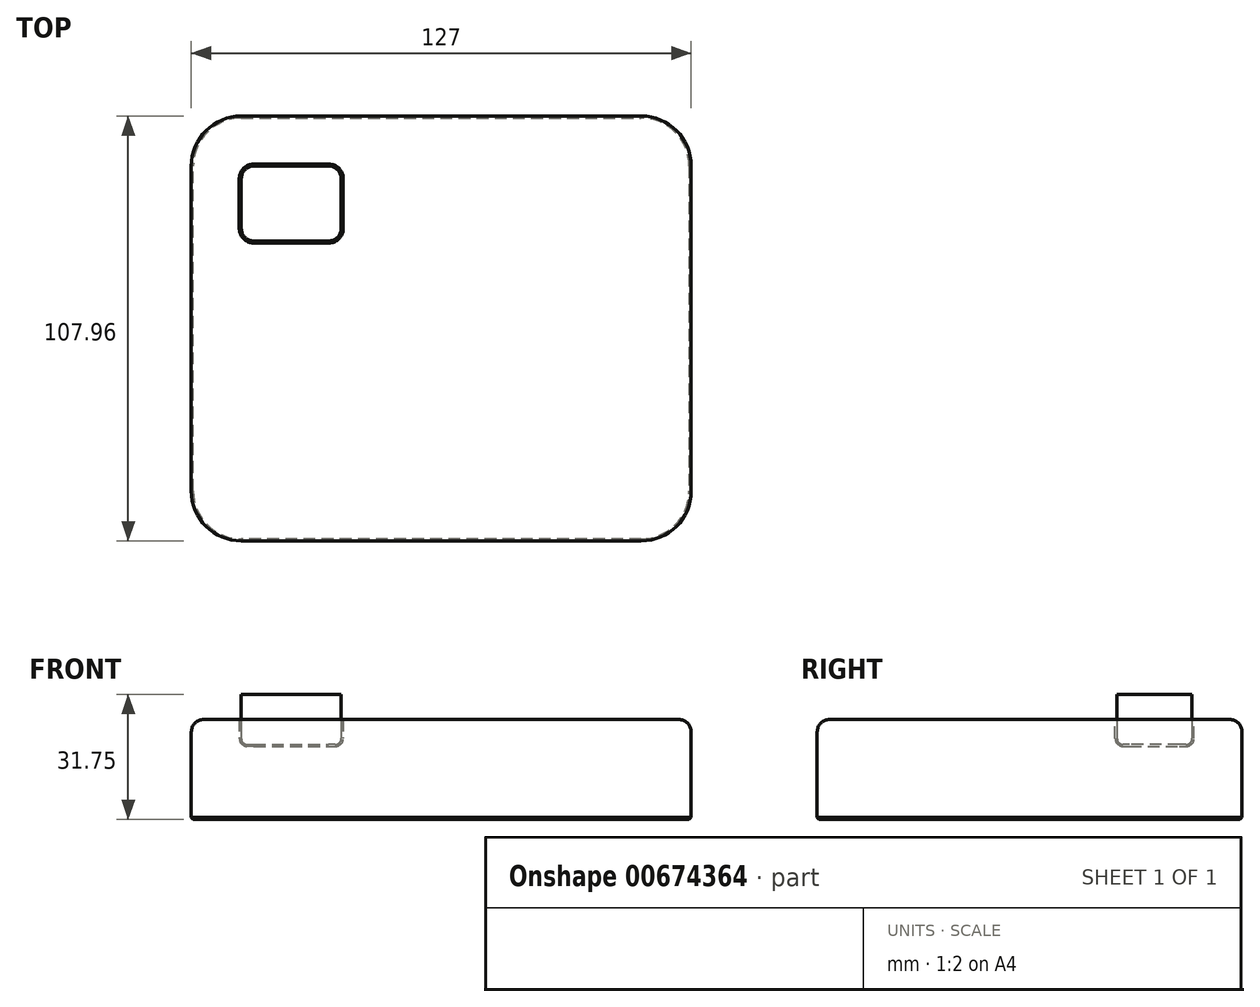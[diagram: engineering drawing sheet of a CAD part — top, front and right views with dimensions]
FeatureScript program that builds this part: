
annotation { "Feature Type Name" : "Feature", "Feature Type Description" : "" }
export const myFeature = defineFeature(function(context is Context, id is Id, definition is map)
    precondition{}
    {
        {
            var Q0;
            Q0=qCreatedBy(makeId("Top.planeOp"),FACE);
            var sketch = newSketch(context, id + "F0", { "sketchPlane" : qUnion([Q0])});
            skLineSegment(sketch, "E0.bottom", {"start": v(63.5, 53.98) * mm, "end": v(-63.5, 53.98) * mm});
            skLineSegment(sketch, "E0.top", {"start": v(63.5, -53.97) * mm, "end": v(-63.5, -53.97) * mm});
            skLineSegment(sketch, "E0.left", {"start": v(63.5, 53.98) * mm, "end": v(63.5, -53.98) * mm});
            skLineSegment(sketch, "E0.right", {"start": v(-63.5, 53.98) * mm, "end": v(-63.5, -53.97) * mm});
            skPoint(sketch, "E0.middle", {"position": v(0, 0) * mm});
            skSolve(sketch);
        }
        {
            var Q0;
            Q0=makeQuery(id+"F0.imprint","IMPRINT",FACE,{"disambiguationData":[TD([[makeQuery(id+"F0.imprint","IMPRINT",EDGE,{"derivedFrom":sQuery(id+"F0.wireOp",EDGE,"E0.bottom")}),1.0]])]});
            extrude(context, id + "F1", {"entities" : qUnion([Q0]), "depth" : 25.4 * mm});
        }
        {
            var Q0;
            Q0=makeQuery(id+"F1.opExtrude","CAP_FACE",FACE,{"disambiguationData":[OSD([sQuery(id+"F0.wireOp",EDGE,"E0.bottom"),sQuery(id+"F0.wireOp",EDGE,"E0.top"),sQuery(id+"F0.wireOp",EDGE,"E0.left"),sQuery(id+"F0.wireOp",EDGE,"E0.right")])],"isStart":false});
            var sketch = newSketch(context, id + "F2", { "sketchPlane" : qUnion([Q0])});
            skLineSegment(sketch, "E1.bottom", {"start": v(-50.8, 41.28) * mm, "end": v(-25.4, 41.28) * mm});
            skLineSegment(sketch, "E1.top", {"start": v(-50.8, 22.23) * mm, "end": v(-25.4, 22.23) * mm});
            skLineSegment(sketch, "E1.left", {"start": v(-50.8, 41.28) * mm, "end": v(-50.8, 22.23) * mm});
            skLineSegment(sketch, "E1.right", {"start": v(-25.4, 41.28) * mm, "end": v(-25.4, 22.23) * mm});
            skSolve(sketch);
        }
        {
            var Q0;
            Q0=qSketchRegion(id+"F2",true);
            extrude(context, id + "F3", {"entities" : qUnion([Q0]), "depth" : 12.7 * mm, "offsetDistance" : 25.4 * mm, "symmetric" : true});
        }
        {
            var Q0;
            Q0=makeQuery(id+"F3.opExtrude","SWEPT_EDGE",EDGE,{"disambiguationData":[OSD([sQuery(id+"F2.wireOp",EDGE,"E1.bottom"),sQuery(id+"F2.wireOp",EDGE,"E1.right")])]});
            var Q1;
            Q1=makeQuery(id+"F3.opExtrude","SWEPT_EDGE",EDGE,{"disambiguationData":[OSD([sQuery(id+"F2.wireOp",EDGE,"E1.top"),sQuery(id+"F2.wireOp",EDGE,"E1.right")])]});
            var Q2;
            Q2=makeQuery(id+"F3.opExtrude","SWEPT_EDGE",EDGE,{"disambiguationData":[OSD([sQuery(id+"F2.wireOp",EDGE,"E1.top"),sQuery(id+"F2.wireOp",EDGE,"E1.left")])]});
            var Q3;
            Q3=makeQuery(id+"F3.opExtrude","SWEPT_EDGE",EDGE,{"disambiguationData":[OSD([sQuery(id+"F2.wireOp",EDGE,"E1.bottom"),sQuery(id+"F2.wireOp",EDGE,"E1.left")])]});
            fillet(context, id + "F4", {"entities" : qUnion([Q0, Q1, Q2, Q3]), "radius" : 3.17 * mm, "tangentPropagation" : true, "allowEdgeOverflow" : false});
        }
        {
            var Q0;
            Q0=makeQuery(id+"F3.opExtrude","CAP_EDGE",EDGE,{"disambiguationData":[OSD([sQuery(id+"F2.wireOp",EDGE,"E1.top")])],"isStart":true});
            fillet(context, id + "F5", {"entities" : qUnion([Q0]), "radius" : 1.52 * mm, "tangentPropagation" : true, "allowEdgeOverflow" : false});
        }
        {
            var Q0;
            Q0=makeQuery(id+"F1.opExtrude","SWEPT_EDGE",EDGE,{"disambiguationData":[OSD([sQuery(id+"F0.wireOp",EDGE,"E0.top"),sQuery(id+"F0.wireOp",EDGE,"E0.left")])]});
            var Q1;
            Q1=makeQuery(id+"F1.opExtrude","SWEPT_EDGE",EDGE,{"disambiguationData":[OSD([sQuery(id+"F0.wireOp",EDGE,"E0.bottom"),sQuery(id+"F0.wireOp",EDGE,"E0.left")])]});
            var Q2;
            Q2=makeQuery(id+"F1.opExtrude","SWEPT_EDGE",EDGE,{"disambiguationData":[OSD([sQuery(id+"F0.wireOp",EDGE,"E0.bottom"),sQuery(id+"F0.wireOp",EDGE,"E0.right")])]});
            var Q3;
            Q3=makeQuery(id+"F1.opExtrude","SWEPT_EDGE",EDGE,{"disambiguationData":[OSD([sQuery(id+"F0.wireOp",EDGE,"E0.top"),sQuery(id+"F0.wireOp",EDGE,"E0.right")])]});
            fillet(context, id + "F6", {"entities" : qUnion([Q0, Q1, Q2, Q3]), "radius" : 12.7 * mm, "tangentPropagation" : true, "allowEdgeOverflow" : false});
        }
        {
            var Q0;
            Q0=makeQuery(id+"F1.opExtrude","CAP_EDGE",EDGE,{"disambiguationData":[OSD([sQuery(id+"F0.wireOp",EDGE,"E0.top")])],"isStart":false});
            fillet(context, id + "F7", {"entities" : qUnion([Q0]), "radius" : 3.17 * mm, "tangentPropagation" : true, "allowEdgeOverflow" : false});
        }
        {
            var Q0;
            Q0=makeQuery(id+"F1.opExtrude","CAP_EDGE",EDGE,{"disambiguationData":[OSD([sQuery(id+"F0.wireOp",EDGE,"E0.top")])],"isStart":true});
            chamfer(context, id + "F8", {"entities" : qUnion([Q0]), "width" : 0.5 * mm, "tangentPropagation" : true});
        }
        {
            var Q0;
            Q0=makeQuery(id+"F3.opExtrude","SWEPT_BODY",BODY,{"disambiguationData":[OSD([sQuery(id+"F2.wireOp",EDGE,"E1.bottom"),sQuery(id+"F2.wireOp",EDGE,"E1.top"),sQuery(id+"F2.wireOp",EDGE,"E1.left"),sQuery(id+"F2.wireOp",EDGE,"E1.right")])]});
            var Q1;
            Q1=makeQuery(id+"F1.opExtrude","SWEPT_BODY",BODY,{"disambiguationData":[OSD([sQuery(id+"F0.wireOp",EDGE,"E0.bottom"),sQuery(id+"F0.wireOp",EDGE,"E0.top"),sQuery(id+"F0.wireOp",EDGE,"E0.left"),sQuery(id+"F0.wireOp",EDGE,"E0.right")])]});
            var Q2;
            Q2=makeQuery(id+"F3.opExtrude","CAP_FACE",FACE,{"disambiguationData":[OSD([sQuery(id+"F2.wireOp",EDGE,"E1.bottom"),sQuery(id+"F2.wireOp",EDGE,"E1.top"),sQuery(id+"F2.wireOp",EDGE,"E1.left"),sQuery(id+"F2.wireOp",EDGE,"E1.right")])],"isStart":false});
            var Q3;
            Q3=makeQuery(id+"F1.opExtrude","CAP_FACE",FACE,{"disambiguationData":[OSD([sQuery(id+"F0.wireOp",EDGE,"E0.bottom"),sQuery(id+"F0.wireOp",EDGE,"E0.top"),sQuery(id+"F0.wireOp",EDGE,"E0.left"),sQuery(id+"F0.wireOp",EDGE,"E0.right")])],"isStart":false});
            booleanBodies(context, id + "F9", {"operationType" : BooleanOperationType.SUBTRACTION, "tools" : qUnion([Q0]), "targets" : qUnion([Q1]), "offset" : true, "offsetAll" : true, "entitiesToOffset" : qUnion([Q2, Q3]), "offsetDistance" : 0.5 * mm, "keepTools" : true});
        }
    });
